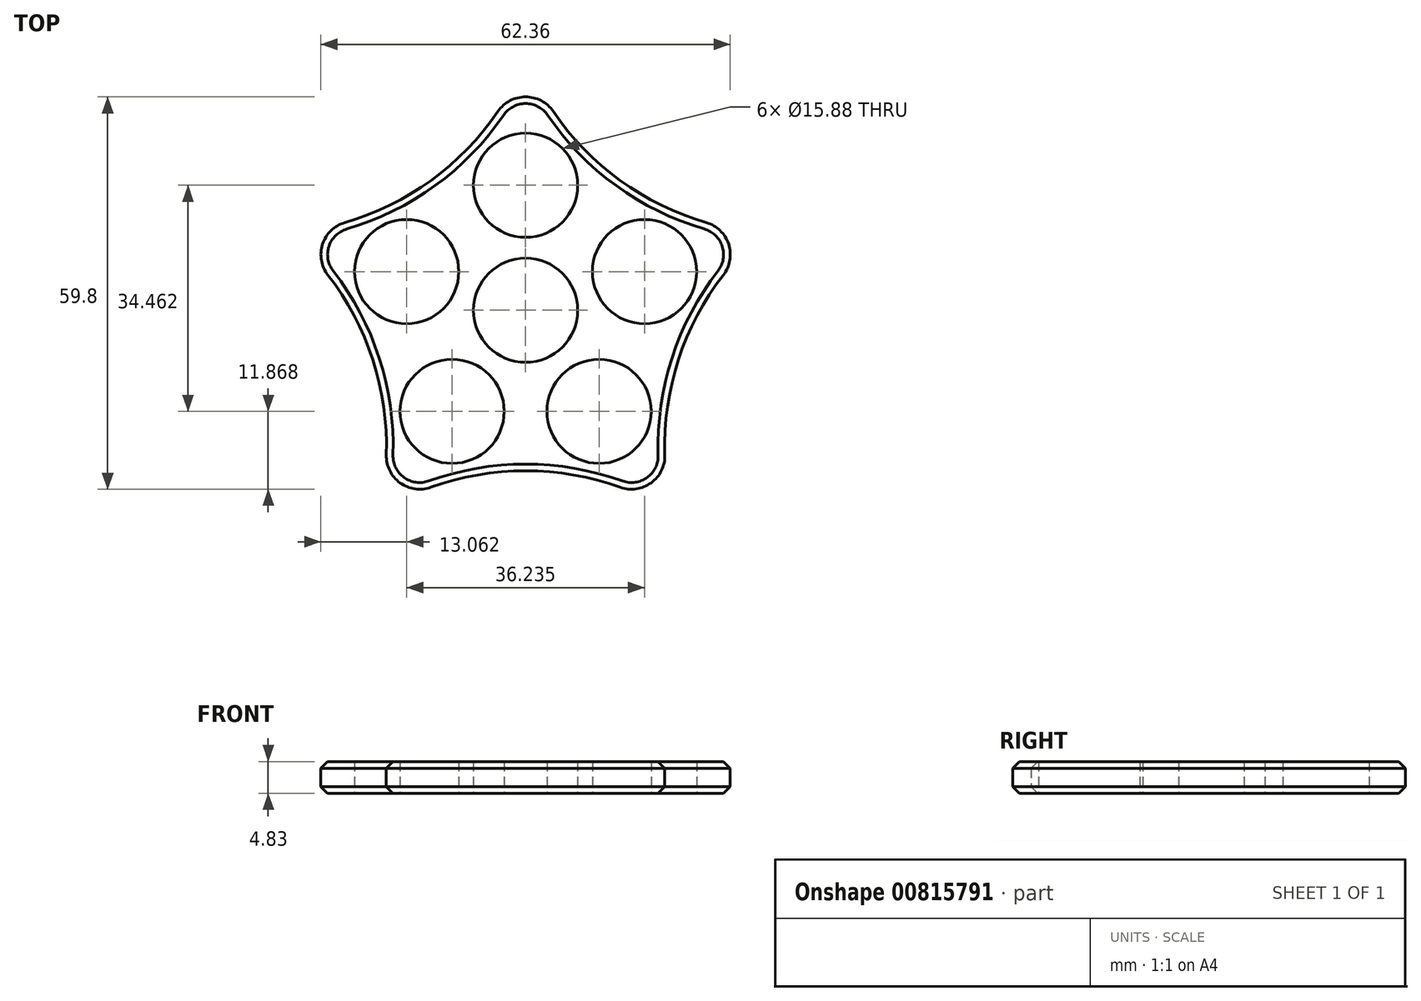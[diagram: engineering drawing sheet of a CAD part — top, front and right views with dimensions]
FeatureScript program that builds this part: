
annotation { "Feature Type Name" : "Feature", "Feature Type Description" : "" }
export const myFeature = defineFeature(function(context is Context, id is Id, definition is map)
    precondition{}
    {
        {
            var Q0;
            Q0=qCreatedBy(makeId("Top.planeOp"),FACE);
            var sketch = newSketch(context, id + "F0", { "sketchPlane" : qUnion([Q0])});
            skCircle(sketch, "E0.cCircle", {"center": v(0, 0) * mm, "radius": 38.1 * mm, "construction": true});
            skLineSegment(sketch, "E0.0", {"start": v(-36.24, 11.77) * mm, "end": v(0, 38.1) * mm, "construction": true});
            skLineSegment(sketch, "E0.1", {"start": v(0, 38.1) * mm, "end": v(36.24, 11.77) * mm, "construction": true});
            skLineSegment(sketch, "E0.2", {"start": v(36.24, 11.77) * mm, "end": v(22.4, -30.82) * mm, "construction": true});
            skLineSegment(sketch, "E0.3", {"start": v(22.4, -30.82) * mm, "end": v(-22.4, -30.82) * mm, "construction": true});
            skLineSegment(sketch, "E0.4", {"start": v(-22.4, -30.82) * mm, "end": v(-36.24, 11.77) * mm, "construction": true});
            skLineSegment(sketch, "E1", {"start": v(0, 0) * mm, "end": v(-29.31, -9.52) * mm, "construction": true});
            skPoint(sketch, "E2", {"position": v(-29.31, -9.52) * mm});
            skArc(sketch, "E3", {"start": v(-22.4, -30.82) * mm, "mid": v(-23.28, -7.56) * mm, "end": v(-36.24, 11.77) * mm});
            skArc(sketch, "E4.1.0", {"start": v(22.4, -30.82) * mm, "mid": v(0, -24.47) * mm, "end": v(-22.4, -30.82) * mm});
            skArc(sketch, "E4.2.0", {"start": v(36.24, 11.77) * mm, "mid": v(23.28, -7.56) * mm, "end": v(22.4, -30.82) * mm});
            skLineSegment(sketch, "E4.2.1", {"start": v(0, 0) * mm, "end": v(29.31, -9.53) * mm, "construction": true});
            skArc(sketch, "E4.3.0", {"start": v(0, 38.1) * mm, "mid": v(14.39, 19.8) * mm, "end": v(36.24, 11.77) * mm});
            skLineSegment(sketch, "E4.3.1", {"start": v(0, 0) * mm, "end": v(18.12, 24.94) * mm, "construction": true});
            skArc(sketch, "E4.4.0", {"start": v(-36.24, 11.77) * mm, "mid": v(-14.39, 19.8) * mm, "end": v(0, 38.1) * mm});
            skLineSegment(sketch, "E4.4.1", {"start": v(0, 0) * mm, "end": v(-18.12, 24.94) * mm, "construction": true});
            skLineSegment(sketch, "E5", {"start": v(0, 0) * mm, "end": v(0, -30.82) * mm, "construction": true});
            skCircle(sketch, "E6", {"center": v(0, 0) * mm, "radius": 7.94 * mm});
            skCircle(sketch, "E7", {"center": v(-18.12, 5.89) * mm, "radius": 7.94 * mm});
            skCircle(sketch, "E8.1.0", {"center": v(-11.2, -15.41) * mm, "radius": 7.94 * mm});
            skCircle(sketch, "E8.2.0", {"center": v(11.2, -15.41) * mm, "radius": 7.94 * mm});
            skCircle(sketch, "E8.3.0", {"center": v(18.12, 5.89) * mm, "radius": 7.94 * mm});
            skCircle(sketch, "E8.4.0", {"center": v(0, 19.05) * mm, "radius": 7.94 * mm});
            skLineSegment(sketch, "E9", {"start": v(0, 0) * mm, "end": v(-18.12, 5.89) * mm, "construction": true});
            skLineSegment(sketch, "E10", {"start": v(0, 0) * mm, "end": v(-11.2, -15.41) * mm, "construction": true});
            skLineSegment(sketch, "E11", {"start": v(11.2, -15.41) * mm, "end": v(0, 0) * mm, "construction": true});
            skSolve(sketch);
        }
        {
            var Q0;
            Q0 = qSketchRegion(id + "F0", true);
            extrude(context, id + "F1", {"entities" : qUnion([Q0]), "depth" : 4.83 * mm, "offsetDistance" : 25.4 * mm});
        }
        {
            var Q0;
            Q0=makeQuery(id+"F1.opExtrude","SWEPT_EDGE",EDGE,{"disambiguationData":[OSD([sQuery(id+"F0.wireOp",EDGE,"E4.3.0"),sQuery(id+"F0.wireOp",EDGE,"E4.4.0")])]});
            var Q1;
            Q1=makeQuery(id+"F1.opExtrude","SWEPT_EDGE",EDGE,{"disambiguationData":[OSD([sQuery(id+"F0.wireOp",EDGE,"E4.2.0"),sQuery(id+"F0.wireOp",EDGE,"E4.3.0")])]});
            var Q2;
            Q2=makeQuery(id+"F1.opExtrude","SWEPT_EDGE",EDGE,{"disambiguationData":[OSD([sQuery(id+"F0.wireOp",EDGE,"E4.1.0"),sQuery(id+"F0.wireOp",EDGE,"E4.2.0")])]});
            var Q3;
            Q3=makeQuery(id+"F1.opExtrude","SWEPT_EDGE",EDGE,{"disambiguationData":[OSD([sQuery(id+"F0.wireOp",EDGE,"E3"),sQuery(id+"F0.wireOp",EDGE,"E4.1.0")])]});
            var Q4;
            Q4=makeQuery(id+"F1.opExtrude","SWEPT_EDGE",EDGE,{"disambiguationData":[OSD([sQuery(id+"F0.wireOp",EDGE,"E3"),sQuery(id+"F0.wireOp",EDGE,"E4.4.0")])]});
            fillet(context, id + "F2", {"entities" : qUnion([Q0, Q1, Q2, Q3, Q4]), "radius" : 5.08 * mm, "tangentPropagation" : true, "allowEdgeOverflow" : false});
        }
        {
            var Q0;
            {var subQ0=sQuery(id+"F0.wireOp",EDGE,"E4.4.0");var subQ1=sQuery(id+"F0.wireOp",EDGE,"E3");Q0=makeQuery(id+"F2.opFillet","BLEND_EDGE",EDGE,{"blendedFrom":[makeQuery(id+"F1.opExtrude","SWEPT_EDGE",EDGE,{"disambiguationData":[OSD([subQ1,subQ0])]}),makeQuery(id+"F1.opExtrude","CAP_FACE",FACE,{"disambiguationData":[OSD([subQ1,sQuery(id+"F0.wireOp",EDGE,"E4.1.0"),sQuery(id+"F0.wireOp",EDGE,"E4.2.0"),sQuery(id+"F0.wireOp",EDGE,"E4.3.0"),subQ0,sQuery(id+"F0.wireOp",EDGE,"E6"),sQuery(id+"F0.wireOp",EDGE,"E7"),sQuery(id+"F0.wireOp",EDGE,"E8.1.0"),sQuery(id+"F0.wireOp",EDGE,"E8.2.0"),sQuery(id+"F0.wireOp",EDGE,"E8.3.0"),sQuery(id+"F0.wireOp",EDGE,"E8.4.0")])],"isStart":true})],"blendedInto":[makeQuery(id+"F1.opExtrude","CAP_FACE",FACE,{"disambiguationData":[OSD([subQ1,sQuery(id+"F0.wireOp",EDGE,"E4.1.0"),sQuery(id+"F0.wireOp",EDGE,"E4.2.0"),sQuery(id+"F0.wireOp",EDGE,"E4.3.0"),subQ0,sQuery(id+"F0.wireOp",EDGE,"E6"),sQuery(id+"F0.wireOp",EDGE,"E7"),sQuery(id+"F0.wireOp",EDGE,"E8.1.0"),sQuery(id+"F0.wireOp",EDGE,"E8.2.0"),sQuery(id+"F0.wireOp",EDGE,"E8.3.0"),sQuery(id+"F0.wireOp",EDGE,"E8.4.0")])],"isStart":true})]});}
            var Q1;
            Q1=makeQuery(id+"F1.opExtrude","CAP_EDGE",EDGE,{"disambiguationData":[OSD([sQuery(id+"F0.wireOp",EDGE,"E3")])],"isStart":false});
            chamfer(context, id + "F3", {"entities" : qUnion([Q0, Q1]), "width" : 1.02 * mm, "tangentPropagation" : true});
        }
    });
